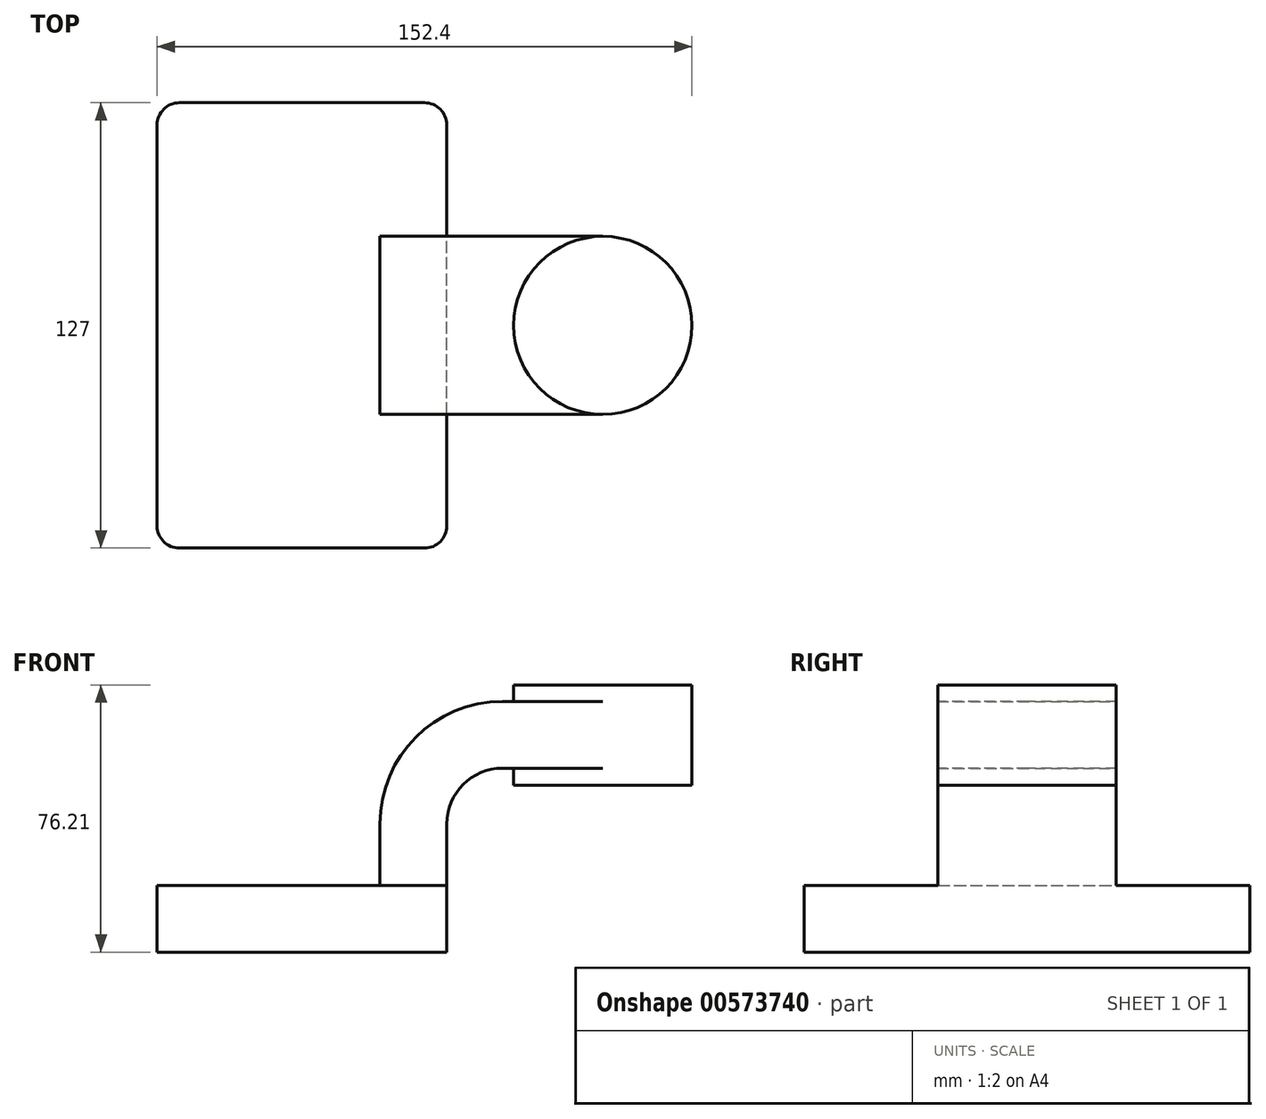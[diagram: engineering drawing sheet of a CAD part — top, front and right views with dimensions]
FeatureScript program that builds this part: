
annotation { "Feature Type Name" : "Feature", "Feature Type Description" : "" }
export const myFeature = defineFeature(function(context is Context, id is Id, definition is map)
    precondition{}
    {
        {
            var Q0;
            Q0=qCreatedBy(makeId("Front.planeOp"),FACE);
            var sketch = newSketch(context, id + "F0", { "sketchPlane" : qUnion([Q0])});
            skLineSegment(sketch, "E0.bottom", {"start": v(-41.27, -9.53) * mm, "end": v(41.28, -9.53) * mm});
            skLineSegment(sketch, "E0.top", {"start": v(-41.28, 9.53) * mm, "end": v(41.28, 9.53) * mm});
            skLineSegment(sketch, "E0.left", {"start": v(-41.28, -9.53) * mm, "end": v(-41.28, 9.53) * mm});
            skLineSegment(sketch, "E0.right", {"start": v(41.28, -9.53) * mm, "end": v(41.28, 9.53) * mm});
            skPoint(sketch, "E0.middle", {"position": v(0, 0) * mm});
            skLineSegment(sketch, "E1.bottom", {"start": v(60.32, 38.1) * mm, "end": v(111.12, 38.1) * mm});
            skLineSegment(sketch, "E1.top", {"start": v(60.32, 66.67) * mm, "end": v(111.12, 66.67) * mm});
            skLineSegment(sketch, "E1.left", {"start": v(60.32, 38.1) * mm, "end": v(60.32, 66.67) * mm});
            skLineSegment(sketch, "E1.right", {"start": v(111.12, 38.1) * mm, "end": v(111.12, 66.67) * mm});
            skPoint(sketch, "E1.middle", {"position": v(85.72, 52.39) * mm});
            skLineSegment(sketch, "E2", {"start": v(41.28, 9.53) * mm, "end": v(41.28, 27.05) * mm});
            skArc(sketch, "E3", {"start": v(41.27, 27.05) * mm, "mid": v(45.92, 38.28) * mm, "end": v(57.15, 42.93) * mm});
            skLineSegment(sketch, "E4", {"start": v(57.15, 42.93) * mm, "end": v(85.72, 42.93) * mm});
            skLineSegment(sketch, "E5.0", {"start": v(57.15, 61.98) * mm, "end": v(85.72, 61.98) * mm});
            skArc(sketch, "E5.1", {"start": v(22.22, 27.05) * mm, "mid": v(32.45, 51.75) * mm, "end": v(57.15, 61.98) * mm});
            skLineSegment(sketch, "E5.2", {"start": v(22.22, 9.53) * mm, "end": v(22.22, 27.05) * mm});
            skLineSegment(sketch, "E6", {"start": v(85.72, 38.1) * mm, "end": v(85.72, 66.67) * mm});
            skFitSpline(sketch, "E7", {"points": [v(-41.27, 9.53) * mm, v(60.32, 61.98) * mm], "startDerivative": vector(0.6, 69.78) * mm, "endDerivative": vector(86.94, -21.6) * mm});
            skSolve(sketch);
        }
        {
            var Q0;
            Q0=makeQuery(id+"F0.imprint","IMPRINT",FACE,{"disambiguationData":[TD([[makeQuery(id+"F0.imprint","IMPRINT",EDGE,{"derivedFrom":sQuery(id+"F0.wireOp",EDGE,"E0.bottom")}),1.0]])]});
            extrude(context, id + "F1", {"entities" : qUnion([Q0]), "endBound" : BoundingType.SYMMETRIC, "depth" : 127 * mm, "offsetDistance" : 25.4 * mm});
        }
        {
            var Q0;
            {var subQ1=sQuery(id+"F0.wireOp",EDGE,"E2");Q0=makeQuery(id+"F0.imprint","IMPRINT",FACE,{"disambiguationData":[TD([[makeQuery(id+"F0.imprint","IMPRINT",EDGE,{"derivedFrom":subQ1}),1.0]])]});}
            var Q1;
            {var subQ3=sQuery(id+"F0.wireOp",EDGE,"E4");var subQ5=sQuery(id+"F0.wireOp",EDGE,"E6");var subQ6=makeQuery(id+"F0.imprint","INTERSECT",VERTEX,{"derivedFrom":[subQ3,subQ5]});Q1=makeQuery(id+"F0.imprint","IMPRINT",FACE,{"disambiguationData":[TD([[makeQuery(id+"F0.imprint","IMPRINT",EDGE,{"disambiguationData":[TD([[subQ6,1.0]])],"derivedFrom":subQ3}),1.0]])]});}
            extrude(context, id + "F2", {"entities" : qUnion([Q0, Q1]), "operationType" : NewBodyOperationType.ADD, "endBound" : BoundingType.SYMMETRIC, "depth" : 50.8 * mm, "offsetDistance" : 25.4 * mm});
        }
        {
            var Q0;
            {var subQ1=sQuery(id+"F0.wireOp",EDGE,"E5.1");Q0=makeQuery(id+"F0.imprint","IMPRINT",FACE,{"disambiguationData":[TD([[makeQuery(id+"F0.imprint","IMPRINT",EDGE,{"derivedFrom":subQ1}),1.0]])]});}
            extrude(context, id + "F3", {"entities" : qUnion([Q0]), "operationType" : NewBodyOperationType.ADD, "endBound" : BoundingType.SYMMETRIC, "depth" : 15.88 * mm, "offsetDistance" : 25.4 * mm});
        }
        {
            var Q0;
            Q0=makeQuery(id+"F1.opExtrude","CAP_EDGE",EDGE,{"disambiguationData":[OSD([sQuery(id+"F0.wireOp",EDGE,"E0.right")])],"isStart":false});
            var Q1;
            Q1=makeQuery(id+"F1.opExtrude","CAP_EDGE",EDGE,{"disambiguationData":[OSD([sQuery(id+"F0.wireOp",EDGE,"E0.right")])],"isStart":true});
            var Q2;
            Q2=makeQuery(id+"F1.opExtrude","CAP_EDGE",EDGE,{"disambiguationData":[OSD([sQuery(id+"F0.wireOp",EDGE,"E0.left")])],"isStart":true});
            var Q3;
            Q3=makeQuery(id+"F1.opExtrude","CAP_EDGE",EDGE,{"disambiguationData":[OSD([sQuery(id+"F0.wireOp",EDGE,"E0.left")])],"isStart":false});
            fillet(context, id + "F4", {"entities" : qUnion([Q0, Q1, Q2, Q3]), "radius" : 6.35 * mm, "tangentPropagation" : true, "allowEdgeOverflow" : false});
        }
        {
            var Q0;
            {var subQ0=sQuery(id+"F0.wireOp",EDGE,"E1.right");Q0=makeQuery(id+"F0.imprint","IMPRINT",FACE,{"disambiguationData":[TD([[makeQuery(id+"F0.imprint","IMPRINT",EDGE,{"derivedFrom":subQ0}),1.0]])]});}
            var Q1;
            Q1=sQuery(id+"F0.wireOp",EDGE,"E6");
            revolve(context, id + "F5", {"operationType" : NewBodyOperationType.ADD, "entities" : qUnion([Q0]), "axis" : qUnion([Q1]), "revolveType" : RevolveType.FULL});
        }
    });
